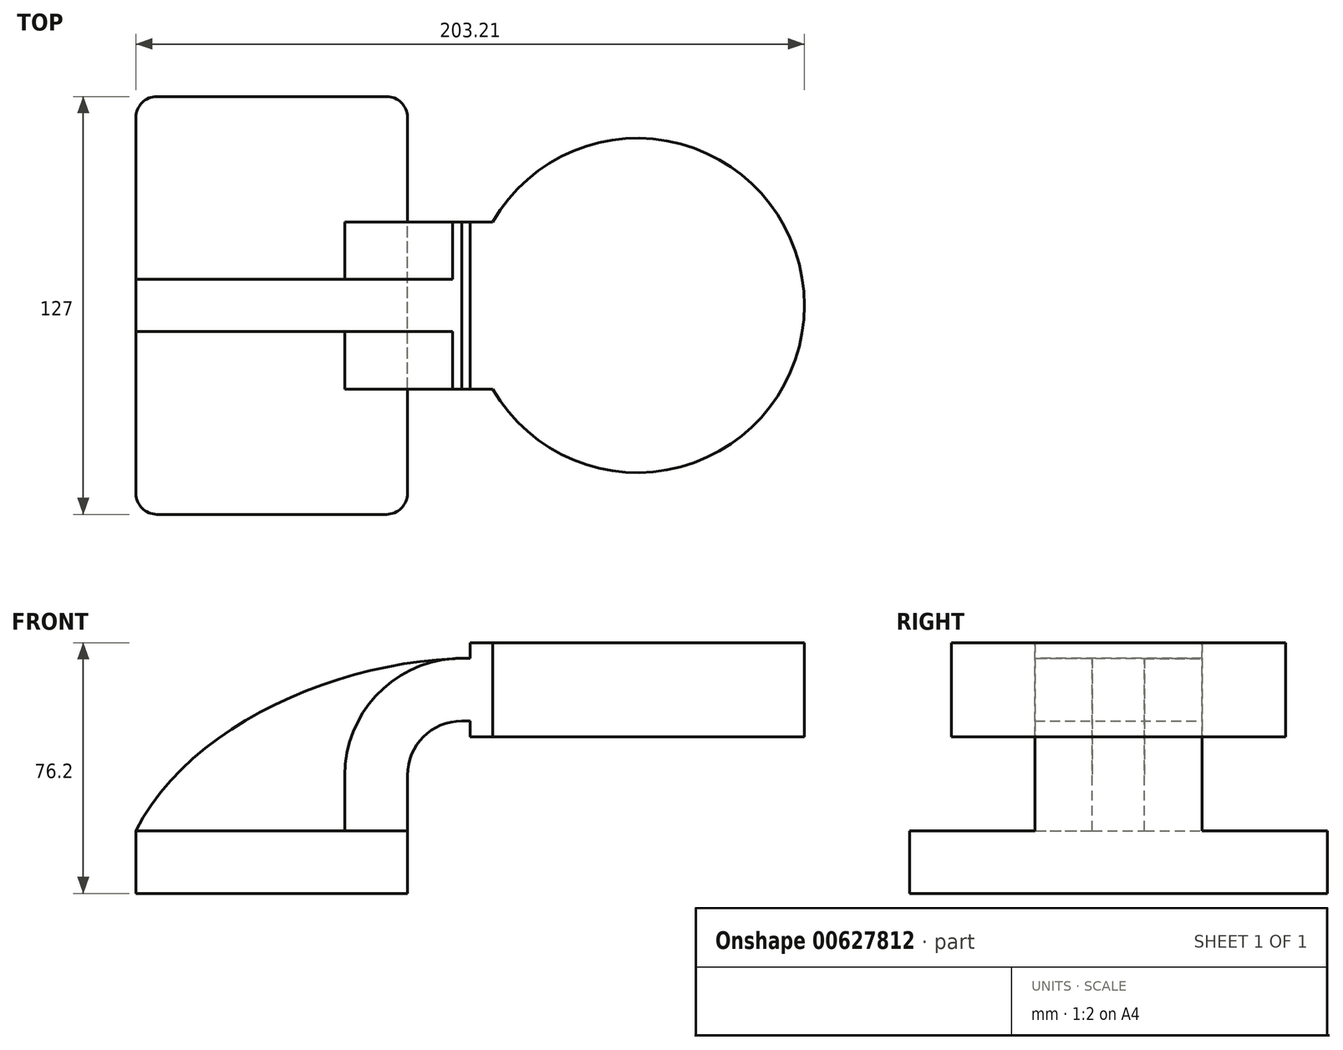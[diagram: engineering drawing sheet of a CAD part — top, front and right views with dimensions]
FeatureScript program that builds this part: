
annotation { "Feature Type Name" : "Feature", "Feature Type Description" : "" }
export const myFeature = defineFeature(function(context is Context, id is Id, definition is map)
    precondition{}
    {
        {
            var Q0;
            Q0=qCreatedBy(makeId("Front.planeOp"),FACE);
            var sketch = newSketch(context, id + "F0", { "sketchPlane" : qUnion([Q0])});
            skLineSegment(sketch, "E0.bottom", {"start": v(-41.28, 9.52) * mm, "end": v(41.27, 9.53) * mm});
            skLineSegment(sketch, "E0.top", {"start": v(-41.28, -9.53) * mm, "end": v(41.28, -9.53) * mm});
            skLineSegment(sketch, "E0.left", {"start": v(-41.28, 9.52) * mm, "end": v(-41.28, -9.53) * mm});
            skLineSegment(sketch, "E0.right", {"start": v(41.27, 9.53) * mm, "end": v(41.28, -9.52) * mm});
            skPoint(sketch, "E0.middle", {"position": v(0, 0) * mm});
            skLineSegment(sketch, "E1.bottom", {"start": v(60.32, 66.68) * mm, "end": v(111.12, 66.68) * mm});
            skLineSegment(sketch, "E1.top", {"start": v(60.32, 38.1) * mm, "end": v(111.12, 38.1) * mm});
            skLineSegment(sketch, "E1.left", {"start": v(60.32, 66.68) * mm, "end": v(60.32, 38.1) * mm});
            skLineSegment(sketch, "E1.right", {"start": v(111.12, 66.68) * mm, "end": v(111.12, 38.1) * mm});
            skPoint(sketch, "E1.middle", {"position": v(85.72, 52.39) * mm});
            skLineSegment(sketch, "E2", {"start": v(41.27, 9.53) * mm, "end": v(41.27, 26.37) * mm});
            skArc(sketch, "E3", {"start": v(41.27, 26.37) * mm, "mid": v(46.11, 38.04) * mm, "end": v(57.78, 42.88) * mm});
            skLineSegment(sketch, "E4", {"start": v(57.78, 42.88) * mm, "end": v(86.1, 42.88) * mm});
            skLineSegment(sketch, "E5.0", {"start": v(57.78, 61.93) * mm, "end": v(86.1, 61.93) * mm});
            skArc(sketch, "E5.1", {"start": v(22.22, 26.37) * mm, "mid": v(32.64, 51.5) * mm, "end": v(57.78, 61.93) * mm});
            skLineSegment(sketch, "E5.2", {"start": v(22.22, 9.53) * mm, "end": v(22.22, 26.37) * mm});
            skFitSpline(sketch, "E6", {"points": [v(-41.28, 9.52) * mm, v(57.78, 61.93) * mm], "startDerivative": vector(48.24, 96.2) * mm, "endDerivative": vector(114, 3.16) * mm});
            skSolve(sketch);
        }
        {
            var Q0;
            Q0=makeQuery(id+"F0.imprint","IMPRINT",FACE,{"disambiguationData":[TD([[makeQuery(id+"F0.imprint","IMPRINT",EDGE,{"derivedFrom":sQuery(id+"F0.wireOp",EDGE,"E0.top")}),1.0]])]});
            extrude(context, id + "F1", {"entities" : qUnion([Q0]), "endBound" : BoundingType.SYMMETRIC, "depth" : 127 * mm, "offsetDistance" : 25.4 * mm});
        }
        {
            var Q0;
            {var subQ1=sQuery(id+"F0.wireOp",EDGE,"E2");Q0=makeQuery(id+"F0.imprint","IMPRINT",FACE,{"disambiguationData":[TD([[makeQuery(id+"F0.imprint","IMPRINT",EDGE,{"derivedFrom":subQ1}),1.0]])]});}
            var Q1;
            {var subQ3=sQuery(id+"F0.wireOp",EDGE,"E1.bottom");Q1=makeQuery(id+"F0.imprint","IMPRINT",FACE,{"disambiguationData":[TD([[makeQuery(id+"F0.imprint","IMPRINT",EDGE,{"derivedFrom":subQ3}),-1.0]])]});}
            extrude(context, id + "F2", {"entities" : qUnion([Q0, Q1]), "operationType" : NewBodyOperationType.ADD, "endBound" : BoundingType.SYMMETRIC, "depth" : 50.8 * mm, "offsetDistance" : 25.4 * mm});
        }
        {
            var Q0;
            {var subQ3=sQuery(id+"F0.wireOp",EDGE,"E5.2");Q0=makeQuery(id+"F0.imprint","IMPRINT",FACE,{"disambiguationData":[TD([[makeQuery(id+"F0.imprint","IMPRINT",EDGE,{"derivedFrom":subQ3}),1.0]])]});}
            extrude(context, id + "F3", {"entities" : qUnion([Q0]), "operationType" : NewBodyOperationType.ADD, "endBound" : BoundingType.SYMMETRIC, "depth" : 15.88 * mm, "offsetDistance" : 25.4 * mm});
        }
        {
            var Q0;
            {var subQ3=sQuery(id+"F0.wireOp",EDGE,"E1.bottom");Q0=makeQuery(id+"F0.imprint","IMPRINT",FACE,{"disambiguationData":[TD([[makeQuery(id+"F0.imprint","IMPRINT",EDGE,{"derivedFrom":subQ3}),-1.0]])]});}
            var Q1;
            Q1=sQuery(id+"F0.wireOp",EDGE,"E1.right");
            revolve(context, id + "F4", {"operationType" : NewBodyOperationType.ADD, "entities" : qUnion([Q0]), "axis" : qUnion([Q1]), "revolveType" : RevolveType.FULL});
        }
        {
            var Q0;
            Q0=makeQuery(id+"F1.opExtrude","CAP_EDGE",EDGE,{"disambiguationData":[OSD([sQuery(id+"F0.wireOp",EDGE,"E0.right")])],"isStart":true});
            var Q1;
            Q1=makeQuery(id+"F1.opExtrude","CAP_EDGE",EDGE,{"disambiguationData":[OSD([sQuery(id+"F0.wireOp",EDGE,"E0.left")])],"isStart":true});
            var Q2;
            Q2=makeQuery(id+"F1.opExtrude","CAP_EDGE",EDGE,{"disambiguationData":[OSD([sQuery(id+"F0.wireOp",EDGE,"E0.right")])],"isStart":false});
            var Q3;
            Q3=makeQuery(id+"F1.opExtrude","CAP_EDGE",EDGE,{"disambiguationData":[OSD([sQuery(id+"F0.wireOp",EDGE,"E0.left")])],"isStart":false});
            fillet(context, id + "F5", {"entities" : qUnion([Q0, Q1, Q2, Q3]), "radius" : 6.35 * mm, "tangentPropagation" : true, "allowEdgeOverflow" : false});
        }
    });
